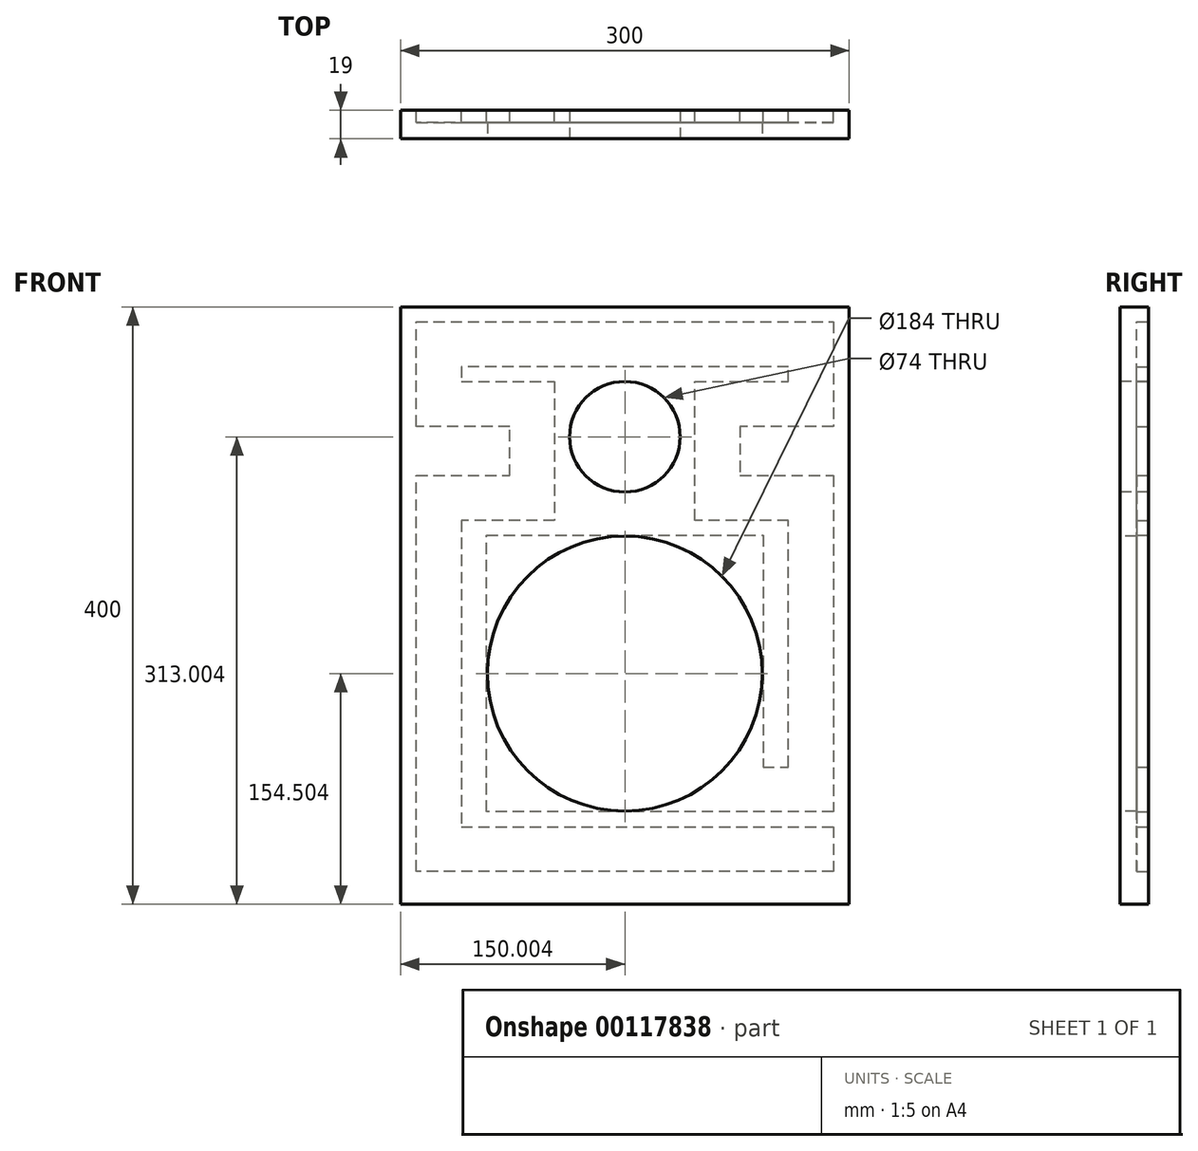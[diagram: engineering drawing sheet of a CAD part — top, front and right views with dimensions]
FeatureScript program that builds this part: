
annotation { "Feature Type Name" : "Feature", "Feature Type Description" : "" }
export const myFeature = defineFeature(function(context is Context, id is Id, definition is map)
    precondition{}
    {
        {
            var Q0;
            Q0=qCreatedBy(makeId("Front.planeOp"),FACE);
            var sketch = newSketch(context, id + "F0", { "sketchPlane" : qUnion([Q0])});
            skLineSegment(sketch, "E0.bottom", {"start": v(-160, 259.67) * mm, "end": v(140, 259.67) * mm});
            skLineSegment(sketch, "E0.top", {"start": v(-160, -140.33) * mm, "end": v(140, -140.33) * mm});
            skLineSegment(sketch, "E0.left", {"start": v(-160, 259.67) * mm, "end": v(-160, -140.33) * mm});
            skLineSegment(sketch, "E0.right", {"start": v(140, 259.67) * mm, "end": v(140, -140.33) * mm});
            skSolve(sketch);
        }
        {
            var Q0;
            Q0 = qSketchRegion(id + "F0", true);
            extrude(context, id + "F1", {"entities" : qUnion([Q0]), "depth" : 19 * mm});
        }
        {
            var Q0;
            Q0=makeQuery(id+"F1.opExtrude","CAP_FACE",FACE,{"disambiguationData":[OSD([sQuery(id+"F0.wireOp",EDGE,"E0.bottom"),sQuery(id+"F0.wireOp",EDGE,"E0.top"),sQuery(id+"F0.wireOp",EDGE,"E0.left"),sQuery(id+"F0.wireOp",EDGE,"E0.right")])],"isStart":false});
            var sketch = newSketch(context, id + "F2", { "sketchPlane" : qUnion([Q0])});
            skCircle(sketch, "E1", {"center": v(-10, 172.67) * mm, "radius": 37 * mm});
            skPoint(sketch, "E1.centerSnap0", {"position": v(-10, 259.67) * mm});
            skCircle(sketch, "E2", {"center": v(-10, 14.17) * mm, "radius": 92 * mm});
            skPoint(sketch, "E2.centerSnap0", {"position": v(-10, -140.33) * mm});
            skSolve(sketch);
        }
        {
            var Q0;
            Q0 = qSketchRegion(id + "F2", true);
            extrude(context, id + "F3", {"entities" : qUnion([Q0]), "operationType" : NewBodyOperationType.REMOVE, "oppositeDirection" : true, "depth" : 19 * mm});
        }
        {
            var Q0;
            Q0=makeQuery(id+"F1.opExtrude","CAP_FACE",FACE,{"disambiguationData":[OSD([sQuery(id+"F0.wireOp",EDGE,"E0.bottom"),sQuery(id+"F0.wireOp",EDGE,"E0.top"),sQuery(id+"F0.wireOp",EDGE,"E0.left"),sQuery(id+"F0.wireOp",EDGE,"E0.right")])],"isStart":true});
            var sketch = newSketch(context, id + "F4", { "sketchPlane" : qUnion([Q0])});
            skLineSegment(sketch, "E3", {"start": v(-129.5, -88.33) * mm, "end": v(-129.5, -118.33) * mm});
            skLineSegment(sketch, "E4", {"start": v(-129.5, -118.33) * mm, "end": v(149.5, -118.33) * mm});
            skLineSegment(sketch, "E5", {"start": v(149.5, -118.33) * mm, "end": v(149.5, 146.67) * mm});
            skLineSegment(sketch, "E6", {"start": v(149.5, 146.67) * mm, "end": v(87, 146.67) * mm});
            skLineSegment(sketch, "E7", {"start": v(87, 146.67) * mm, "end": v(87, 179.67) * mm});
            skLineSegment(sketch, "E8", {"start": v(87, 179.67) * mm, "end": v(149.5, 179.67) * mm});
            skLineSegment(sketch, "E9", {"start": v(149.5, 179.67) * mm, "end": v(149.5, 249.67) * mm});
            skLineSegment(sketch, "E10", {"start": v(149.5, 249.67) * mm, "end": v(-129.5, 249.67) * mm});
            skLineSegment(sketch, "E11", {"start": v(-129.5, 249.67) * mm, "end": v(-129.5, 179.67) * mm});
            skLineSegment(sketch, "E12", {"start": v(-129.5, 179.67) * mm, "end": v(-67, 179.67) * mm});
            skLineSegment(sketch, "E13", {"start": v(-67, 179.67) * mm, "end": v(-67, 146.67) * mm});
            skLineSegment(sketch, "E14", {"start": v(-67, 146.67) * mm, "end": v(-129.5, 146.67) * mm});
            skLineSegment(sketch, "E15", {"start": v(-129.5, 146.67) * mm, "end": v(-129.5, -78.33) * mm});
            skLineSegment(sketch, "E16", {"start": v(-129.5, -78.33) * mm, "end": v(102.5, -78.33) * mm});
            skLineSegment(sketch, "E17", {"start": v(102.5, -78.33) * mm, "end": v(102.5, 106.67) * mm});
            skLineSegment(sketch, "E18", {"start": v(102.5, 106.67) * mm, "end": v(-82.5, 106.67) * mm});
            skLineSegment(sketch, "E19", {"start": v(-82.5, 106.67) * mm, "end": v(-82.5, -48.33) * mm});
            skLineSegment(sketch, "E20", {"start": v(-82.5, -48.33) * mm, "end": v(-99.5, -48.33) * mm});
            skLineSegment(sketch, "E21", {"start": v(-99.5, -48.33) * mm, "end": v(-99.5, 116.67) * mm});
            skLineSegment(sketch, "E22", {"start": v(-99.5, 116.67) * mm, "end": v(-37, 116.67) * mm});
            skLineSegment(sketch, "E23", {"start": v(-37, 116.67) * mm, "end": v(-37, 209.67) * mm});
            skLineSegment(sketch, "E24", {"start": v(-37, 209.67) * mm, "end": v(-99.5, 209.67) * mm});
            skLineSegment(sketch, "E25", {"start": v(-99.5, 209.67) * mm, "end": v(-99.5, 219.67) * mm});
            skLineSegment(sketch, "E26", {"start": v(-99.5, 219.67) * mm, "end": v(119.5, 219.67) * mm});
            skLineSegment(sketch, "E27", {"start": v(119.5, 219.67) * mm, "end": v(119.5, 209.67) * mm});
            skLineSegment(sketch, "E28", {"start": v(119.5, 209.67) * mm, "end": v(57, 209.67) * mm});
            skLineSegment(sketch, "E29", {"start": v(57, 209.67) * mm, "end": v(57, 116.67) * mm});
            skLineSegment(sketch, "E30", {"start": v(57, 116.67) * mm, "end": v(119.5, 116.67) * mm});
            skLineSegment(sketch, "E31", {"start": v(119.5, 116.67) * mm, "end": v(119.5, -88.33) * mm});
            skLineSegment(sketch, "E32", {"start": v(119.5, -88.33) * mm, "end": v(-129.5, -88.33) * mm});
            skSolve(sketch);
        }
        {
            var Q0;
            Q0 = qSketchRegion(id + "F4", true);
            extrude(context, id + "F5", {"entities" : qUnion([Q0]), "operationType" : NewBodyOperationType.REMOVE, "oppositeDirection" : true, "depth" : 8 * mm});
        }
    });
